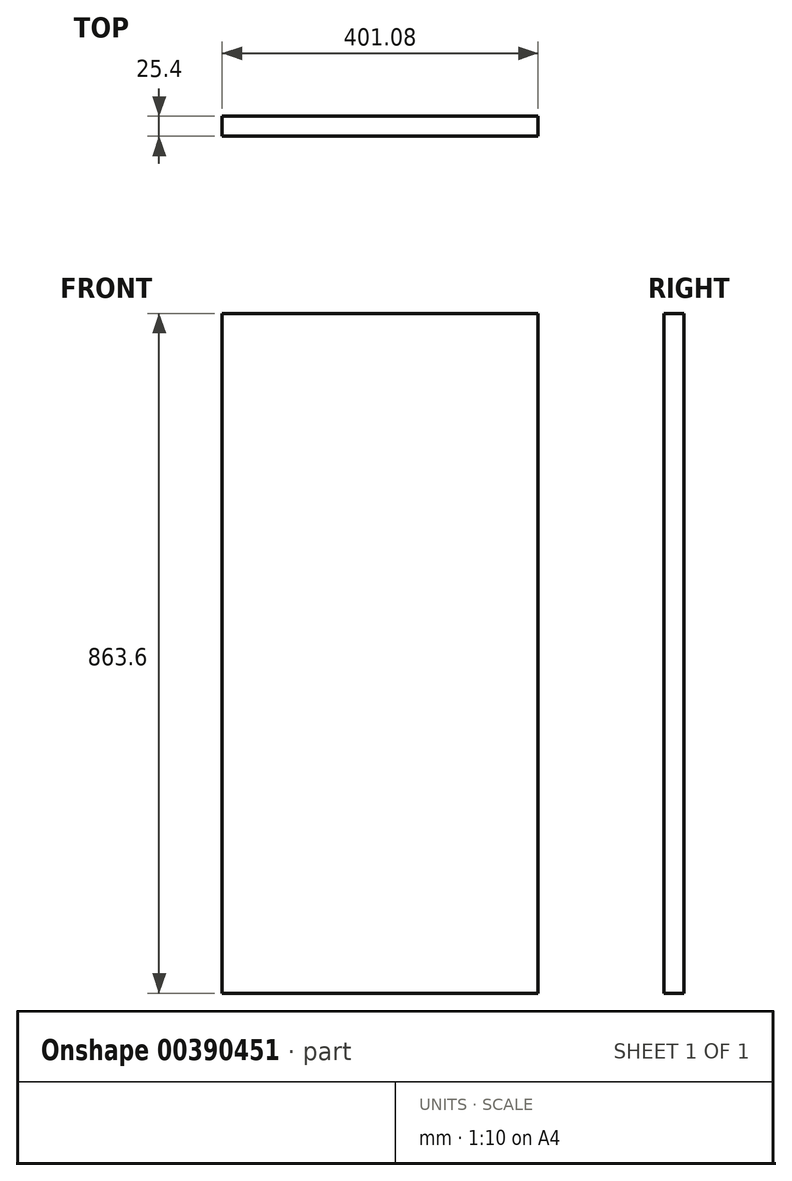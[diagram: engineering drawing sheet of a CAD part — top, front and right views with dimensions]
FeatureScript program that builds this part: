
annotation { "Feature Type Name" : "Feature", "Feature Type Description" : "" }
export const myFeature = defineFeature(function(context is Context, id is Id, definition is map)
    precondition{}
    {
        {
            var Q0;
            Q0=qCreatedBy(makeId("Front.planeOp"),FACE);
            var sketch = newSketch(context, id + "F0", { "sketchPlane" : qUnion([Q0])});
            skLineSegment(sketch, "E0.bottom", {"start": v(-753.25, 412.73) * mm, "end": v(-352.17, 412.73) * mm});
            skLineSegment(sketch, "E0.top", {"start": v(-753.25, -450.87) * mm, "end": v(-352.17, -450.87) * mm});
            skLineSegment(sketch, "E0.left", {"start": v(-753.25, 412.73) * mm, "end": v(-753.25, -450.87) * mm});
            skLineSegment(sketch, "E0.right", {"start": v(-352.17, 412.73) * mm, "end": v(-352.17, -450.87) * mm});
            skSolve(sketch);
        }
        {
            var Q0;
            Q0=makeQuery(id+"F0.imprint","IMPRINT",FACE,{"disambiguationData":[TD([[makeQuery(id+"F0.imprint","IMPRINT",EDGE,{"derivedFrom":sQuery(id+"F0.wireOp",EDGE,"E0.bottom")}),-1.0]])]});
            extrude(context, id + "F1", {"entities" : qUnion([Q0]), "depth" : 25.4 * mm});
        }
    });
